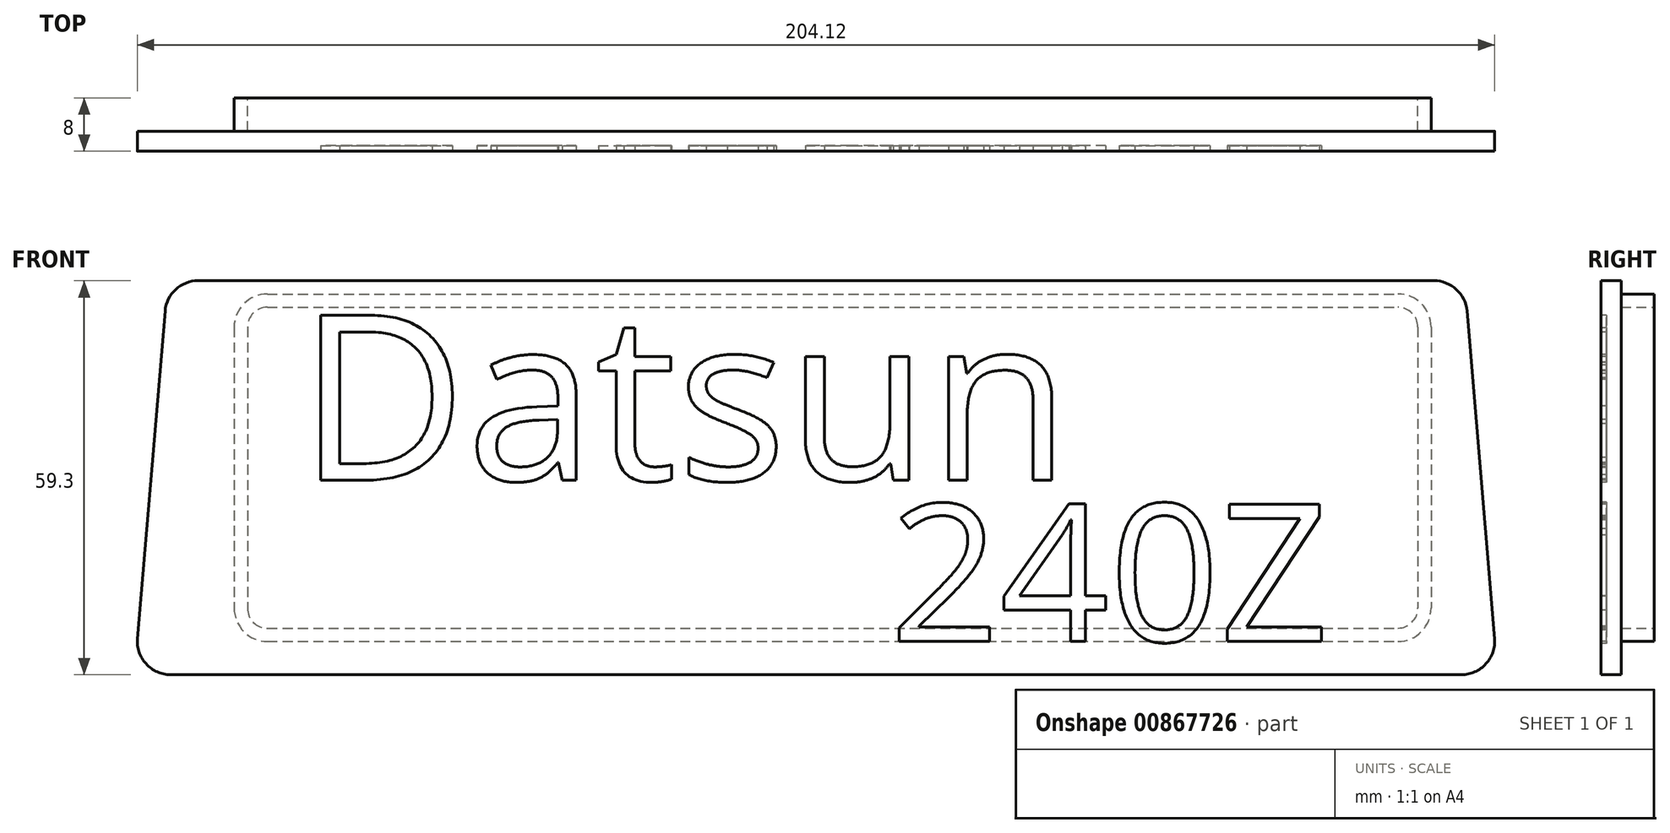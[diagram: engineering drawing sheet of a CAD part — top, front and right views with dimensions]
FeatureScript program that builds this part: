
annotation { "Feature Type Name" : "Feature", "Feature Type Description" : "" }
export const myFeature = defineFeature(function(context is Context, id is Id, definition is map)
    precondition{}
    {
        {
            var Q0;
            Q0=qCreatedBy(makeId("Front.planeOp"),FACE);
            var sketch = newSketch(context, id + "F0", { "sketchPlane" : qUnion([Q0])});
            skLineSegment(sketch, "E0.bottom", {"start": v(-74.37, 26.81) * mm, "end": v(95.63, 26.81) * mm});
            skLineSegment(sketch, "E0.top", {"start": v(-74.37, -25.49) * mm, "end": v(95.63, -25.49) * mm});
            skLineSegment(sketch, "E0.left", {"start": v(-79.37, 21.81) * mm, "end": v(-79.37, -20.49) * mm});
            skLineSegment(sketch, "E0.right", {"start": v(100.63, 21.81) * mm, "end": v(100.63, -20.49) * mm});
            skPoint(sketch, "E1.visualSharp", {"position": v(-79.37, 26.81) * mm});
            skArc(sketch, "E1.filletArc", {"start": v(-74.37, 26.81) * mm, "mid": v(-77.9, 25.35) * mm, "end": v(-79.37, 21.81) * mm});
            skPoint(sketch, "E2.visualSharp", {"position": v(-79.37, -25.49) * mm});
            skArc(sketch, "E2.filletArc", {"start": v(-79.37, -20.49) * mm, "mid": v(-77.9, -24.02) * mm, "end": v(-74.37, -25.49) * mm});
            skPoint(sketch, "E3.visualSharp", {"position": v(100.63, -25.49) * mm});
            skArc(sketch, "E3.filletArc", {"start": v(95.63, -25.49) * mm, "mid": v(99.17, -24.02) * mm, "end": v(100.63, -20.49) * mm});
            skPoint(sketch, "E4.visualSharp", {"position": v(100.63, 26.81) * mm});
            skArc(sketch, "E4.filletArc", {"start": v(100.63, 21.81) * mm, "mid": v(99.17, 25.35) * mm, "end": v(95.63, 26.81) * mm});
            skLineSegment(sketch, "E5.0", {"start": v(98.63, 21.81) * mm, "end": v(98.63, -20.49) * mm});
            skArc(sketch, "E5.1", {"start": v(95.63, -23.49) * mm, "mid": v(97.75, -22.6) * mm, "end": v(98.63, -20.49) * mm});
            skArc(sketch, "E5.2", {"start": v(98.63, 21.81) * mm, "mid": v(97.75, 23.93) * mm, "end": v(95.63, 24.81) * mm});
            skLineSegment(sketch, "E5.3", {"start": v(-74.37, -23.49) * mm, "end": v(95.63, -23.49) * mm});
            skLineSegment(sketch, "E5.4", {"start": v(-74.37, 24.81) * mm, "end": v(95.63, 24.81) * mm});
            skArc(sketch, "E5.5", {"start": v(-74.37, 24.81) * mm, "mid": v(-76.5, 23.93) * mm, "end": v(-77.37, 21.81) * mm});
            skLineSegment(sketch, "E5.6", {"start": v(-77.37, 21.81) * mm, "end": v(-77.37, -20.49) * mm});
            skArc(sketch, "E5.7", {"start": v(-77.37, -20.49) * mm, "mid": v(-76.5, -22.6) * mm, "end": v(-74.37, -23.49) * mm});
            skSolve(sketch);
        }
        {
            var Q0;
            Q0=makeQuery(id+"F0.imprint","IMPRINT",FACE,{"disambiguationData":[TD([[makeQuery(id+"F0.imprint","IMPRINT",EDGE,{"derivedFrom":sQuery(id+"F0.wireOp",EDGE,"E0.bottom")}),-1.0]])]});
            extrude(context, id + "F1", {"entities" : qUnion([Q0]), "depth" : 5 * mm, "offsetDistance" : 25 * mm});
        }
        {
            var Q0;
            Q0=makeQuery(id+"F1.opExtrude","CAP_FACE",FACE,{"disambiguationData":[OSD([sQuery(id+"F0.wireOp",EDGE,"E0.bottom"),sQuery(id+"F0.wireOp",EDGE,"E0.top"),sQuery(id+"F0.wireOp",EDGE,"E0.left"),sQuery(id+"F0.wireOp",EDGE,"E0.right"),sQuery(id+"F0.wireOp",EDGE,"E1.filletArc"),sQuery(id+"F0.wireOp",EDGE,"E2.filletArc"),sQuery(id+"F0.wireOp",EDGE,"E3.filletArc"),sQuery(id+"F0.wireOp",EDGE,"E4.filletArc"),sQuery(id+"F0.wireOp",EDGE,"E5.0"),sQuery(id+"F0.wireOp",EDGE,"E5.1"),sQuery(id+"F0.wireOp",EDGE,"E5.2"),sQuery(id+"F0.wireOp",EDGE,"E5.3"),sQuery(id+"F0.wireOp",EDGE,"E5.4"),sQuery(id+"F0.wireOp",EDGE,"E5.5"),sQuery(id+"F0.wireOp",EDGE,"E5.6"),sQuery(id+"F0.wireOp",EDGE,"E5.7")])],"isStart":false});
            var sketch = newSketch(context, id + "F2", { "sketchPlane" : qUnion([Q0])});
            skLineSegment(sketch, "E6.0", {"start": v(-79.37, 21.81) * mm, "end": v(-79.37, -20.49) * mm, "construction": true});
            skLineSegment(sketch, "E7.0", {"start": v(-74.37, 26.81) * mm, "end": v(95.63, 26.81) * mm, "construction": true});
            skLineSegment(sketch, "E8.0", {"start": v(-74.37, -25.49) * mm, "end": v(95.63, -25.49) * mm, "construction": true});
            skLineSegment(sketch, "E9.0", {"start": v(100.63, 21.81) * mm, "end": v(100.63, -20.49) * mm, "construction": true});
            skLineSegment(sketch, "E10.0", {"start": v(-79.37, 28.81) * mm, "end": v(100.63, 28.81) * mm});
            skLineSegment(sketch, "E11.0", {"start": v(-79.37, -30.49) * mm, "end": v(100.63, -30.49) * mm});
            skLineSegment(sketch, "E12", {"start": v(106.02, 24.23) * mm, "end": v(110.17, -25.07) * mm});
            skLineSegment(sketch, "E13", {"start": v(-89.76, 24.23) * mm, "end": v(-93.91, -25.07) * mm});
            skLineSegment(sketch, "E14", {"start": v(-84.77, 28.81) * mm, "end": v(-79.37, 28.81) * mm});
            skLineSegment(sketch, "E15", {"start": v(-88.93, -30.49) * mm, "end": v(-79.37, -30.49) * mm});
            skLineSegment(sketch, "E16", {"start": v(100.63, -30.49) * mm, "end": v(105.2, -30.49) * mm});
            skLineSegment(sketch, "E17", {"start": v(101.03, 28.81) * mm, "end": v(100.63, 28.81) * mm});
            skPoint(sketch, "E18.visualSharp", {"position": v(-89.37, 28.81) * mm});
            skArc(sketch, "E18.filletArc", {"start": v(-84.77, 28.81) * mm, "mid": v(-88.16, 27.5) * mm, "end": v(-89.76, 24.23) * mm});
            skPoint(sketch, "E19.visualSharp", {"position": v(-94.37, -30.49) * mm});
            skArc(sketch, "E19.filletArc", {"start": v(-93.91, -25.07) * mm, "mid": v(-92.61, -28.87) * mm, "end": v(-88.93, -30.49) * mm});
            skPoint(sketch, "E20.visualSharp", {"position": v(110.63, -30.49) * mm});
            skArc(sketch, "E20.filletArc", {"start": v(105.2, -30.49) * mm, "mid": v(108.87, -28.87) * mm, "end": v(110.17, -25.07) * mm});
            skPoint(sketch, "E21.visualSharp", {"position": v(105.63, 28.81) * mm});
            skArc(sketch, "E21.filletArc", {"start": v(106.02, 24.23) * mm, "mid": v(104.42, 27.5) * mm, "end": v(101.03, 28.81) * mm});
            skSolve(sketch);
        }
        {
            var Q0;
            Q0 = qSketchRegion(id + "F2", true);
            extrude(context, id + "F3", {"entities" : qUnion([Q0]), "operationType" : NewBodyOperationType.ADD, "depth" : 3 * mm, "offsetDistance" : 25 * mm});
        }
        {
            var Q0;
            Q0=makeQuery(id+"F3.opExtrude","CAP_FACE",FACE,{"disambiguationData":[OSD([sQuery(id+"F2.wireOp",EDGE,"E10.0"),sQuery(id+"F2.wireOp",EDGE,"869edc84-cfdb-439c-aa43-73e11c4e65a2.0"),sQuery(id+"F2.wireOp",EDGE,"1815e11f-60c7-42b0-a389-473d3cc2397c.0"),sQuery(id+"F2.wireOp",EDGE,"E11.0"),sQuery(id+"F2.wireOp",EDGE,"fe50adf3-e3ec-45f0-a9d4-904f1c7920eb.filletArc"),sQuery(id+"F2.wireOp",EDGE,"dd863ed3-b084-4396-b3fd-220d2a0eaeb5.filletArc"),sQuery(id+"F2.wireOp",EDGE,"7d8b84a5-0a76-4cfe-a84a-9cee00c68719.filletArc"),sQuery(id+"F2.wireOp",EDGE,"3a402e16-6dbd-4ae4-8043-ae76759780f0.filletArc")])],"isStart":false});
            var sketch = newSketch(context, id + "F4", { "sketchPlane" : qUnion([Q0])});
            skText(sketch, "E22", { "text": "Datsun", "fontName": "OpenSans-Regular.ttf"});
            skText(sketch, "E23", { "text": "240Z", "fontName": "OpenSans-Regular.ttf"});
            skLineSegment(sketch, "E24.0", {"start": v(101.03, 28.81) * mm, "end": v(-84.77, 28.81) * mm, "construction": true});
            skLineSegment(sketch, "E25.0", {"start": v(-88.93, -30.49) * mm, "end": v(105.2, -30.49) * mm, "construction": true});
            skLineSegment(sketch, "E26", {"start": v(-84.77, 28.81) * mm, "end": v(-84.77, -30.49) * mm, "construction": true});
            skLineSegment(sketch, "E27", {"start": v(101.03, 28.81) * mm, "end": v(101.03, -30.49) * mm, "construction": true});
            const initialGuessF4  = {"E22": [-0.06977, -0.00121, 1, 0, 0.02502], "E23": [0.01924, -0.02549, 1, 0, 0.02081]};
            skSetInitialGuess(sketch, initialGuessF4);
            skSolve(sketch);
        }
        {
            var Q0;
            Q0=makeQuery(id+"F4.imprint","IMPRINT",FACE,{"disambiguationData":[TD([[makeQuery(id+"F4.imprint","IMPRINT",EDGE,{"derivedFrom":sQuery(id+"F4.wireOp",EDGE,"E22.sketch_text.stroke-0")}),-1.0]])]});
            var Q1;
            Q1=makeQuery(id+"F4.imprint","IMPRINT",FACE,{"disambiguationData":[TD([[makeQuery(id+"F4.imprint","IMPRINT",EDGE,{"derivedFrom":sQuery(id+"F4.wireOp",EDGE,"E22.sketch_text.stroke-14")}),-1.0]])]});
            var Q2;
            Q2=makeQuery(id+"F4.imprint","IMPRINT",FACE,{"disambiguationData":[TD([[makeQuery(id+"F4.imprint","IMPRINT",EDGE,{"derivedFrom":sQuery(id+"F4.wireOp",EDGE,"E22.sketch_text.stroke-41")}),-1.0]])]});
            var Q3;
            Q3=makeQuery(id+"F4.imprint","IMPRINT",FACE,{"disambiguationData":[TD([[makeQuery(id+"F4.imprint","IMPRINT",EDGE,{"derivedFrom":sQuery(id+"F4.wireOp",EDGE,"E22.sketch_text.stroke-60")}),-1.0]])]});
            var Q4;
            Q4=makeQuery(id+"F4.imprint","IMPRINT",FACE,{"disambiguationData":[TD([[makeQuery(id+"F4.imprint","IMPRINT",EDGE,{"derivedFrom":sQuery(id+"F4.wireOp",EDGE,"E22.sketch_text.stroke-85")}),-1.0]])]});
            var Q5;
            Q5=makeQuery(id+"F4.imprint","IMPRINT",FACE,{"disambiguationData":[TD([[makeQuery(id+"F4.imprint","IMPRINT",EDGE,{"derivedFrom":sQuery(id+"F4.wireOp",EDGE,"E22.sketch_text.stroke-102")}),-1.0]])]});
            var Q6;
            Q6=makeQuery(id+"F4.imprint","IMPRINT",FACE,{"disambiguationData":[TD([[makeQuery(id+"F4.imprint","IMPRINT",EDGE,{"derivedFrom":sQuery(id+"F4.wireOp",EDGE,"E23.sketch_text.stroke-0")}),-1.0]])]});
            var Q7;
            Q7=makeQuery(id+"F4.imprint","IMPRINT",FACE,{"disambiguationData":[TD([[makeQuery(id+"F4.imprint","IMPRINT",EDGE,{"derivedFrom":sQuery(id+"F4.wireOp",EDGE,"E23.sketch_text.stroke-20")}),-1.0]])]});
            var Q8;
            Q8=makeQuery(id+"F4.imprint","IMPRINT",FACE,{"disambiguationData":[TD([[makeQuery(id+"F4.imprint","IMPRINT",EDGE,{"derivedFrom":sQuery(id+"F4.wireOp",EDGE,"E23.sketch_text.stroke-37")}),-1.0]])]});
            var Q9;
            Q9=makeQuery(id+"F4.imprint","IMPRINT",FACE,{"disambiguationData":[TD([[makeQuery(id+"F4.imprint","IMPRINT",EDGE,{"derivedFrom":sQuery(id+"F4.wireOp",EDGE,"E23.sketch_text.stroke-53")}),-1.0]])]});
            extrude(context, id + "F5", {"entities" : qUnion([Q0, Q1, Q2, Q3, Q4, Q5, Q6, Q7, Q8, Q9]), "operationType" : NewBodyOperationType.REMOVE, "oppositeDirection" : true, "depth" : 0.8 * mm, "offsetDistance" : 25 * mm});
        }
    });
